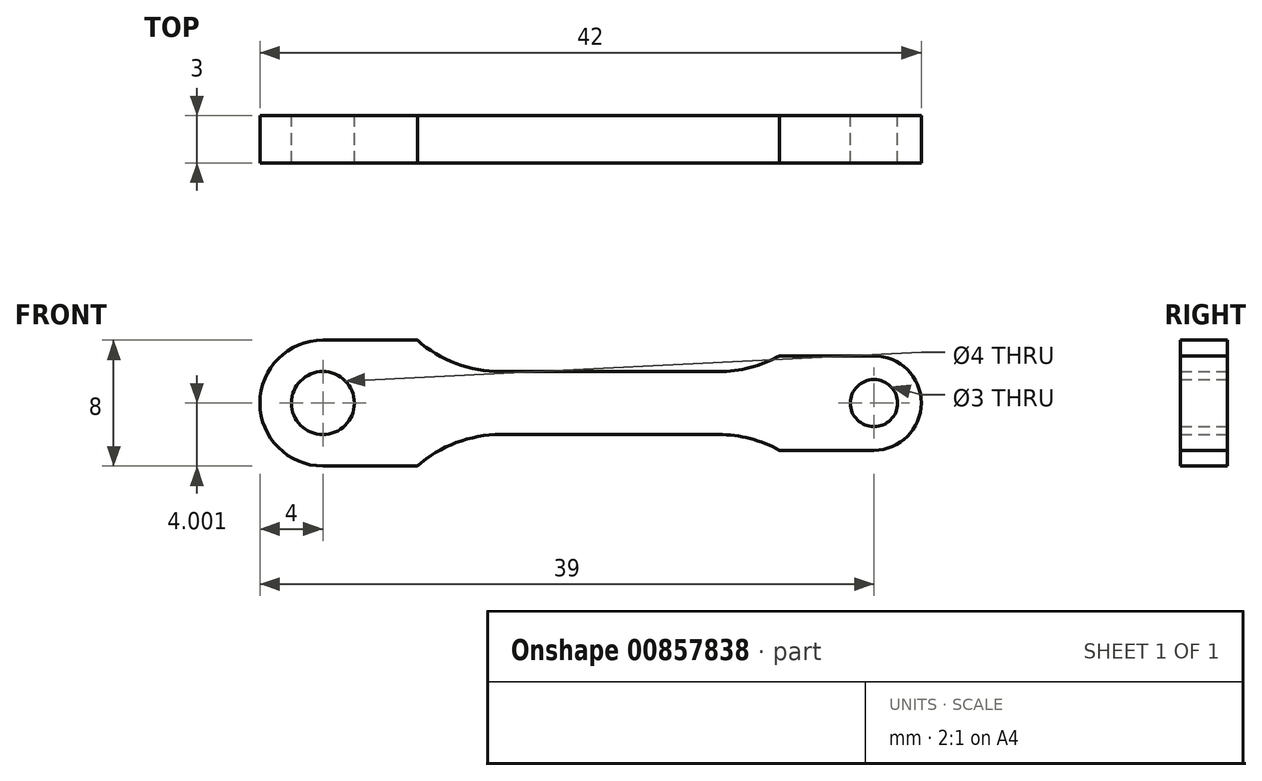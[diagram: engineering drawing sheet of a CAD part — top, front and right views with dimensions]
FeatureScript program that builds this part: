
annotation { "Feature Type Name" : "Feature", "Feature Type Description" : "" }
export const myFeature = defineFeature(function(context is Context, id is Id, definition is map)
    precondition{}
    {
        {
            var Q0;
            Q0=qCreatedBy(makeId("Front.planeOp"),FACE);
            var sketch = newSketch(context, id + "F0", { "sketchPlane" : qUnion([Q0])});
            skCircle(sketch, "E0", {"center": v(22.61, 11.46) * mm, "radius": 2 * mm});
            skCircle(sketch, "E1", {"center": v(57.61, 11.46) * mm, "radius": 1.5 * mm});
            skArc(sketch, "E2", {"start": v(22.61, 15.46) * mm, "mid": v(18.61, 11.46) * mm, "end": v(22.61, 7.46) * mm});
            skArc(sketch, "E3", {"start": v(57.61, 8.46) * mm, "mid": v(60.61, 11.46) * mm, "end": v(57.61, 14.46) * mm});
            skLineSegment(sketch, "E4", {"start": v(22.61, 7.46) * mm, "end": v(28.61, 7.46) * mm});
            skLineSegment(sketch, "E5", {"start": v(22.61, 15.46) * mm, "end": v(28.61, 15.46) * mm});
            skLineSegment(sketch, "E6", {"start": v(57.61, 14.46) * mm, "end": v(51.61, 14.46) * mm});
            skLineSegment(sketch, "E7", {"start": v(57.61, 8.46) * mm, "end": v(51.61, 8.46) * mm});
            skLineSegment(sketch, "E8", {"start": v(22.61, 11.46) * mm, "end": v(67.05, 11.46) * mm, "construction": true});
            skLineSegment(sketch, "E9", {"start": v(33.9, 13.46) * mm, "end": v(47.74, 13.46) * mm});
            skLineSegment(sketch, "E10", {"start": v(33.9, 9.46) * mm, "end": v(47.74, 9.46) * mm});
            skPoint(sketch, "E11", {"position": v(33.9, 1.46) * mm});
            skArc(sketch, "E12", {"start": v(33.9, 9.46) * mm, "mid": v(31.07, 8.94) * mm, "end": v(28.61, 7.46) * mm});
            skPoint(sketch, "E13.MirrorP", {"position": v(33.9, 21.46) * mm});
            skArc(sketch, "E14", {"start": v(33.9, 13.46) * mm, "mid": v(31.07, 13.98) * mm, "end": v(28.61, 15.46) * mm});
            skPoint(sketch, "E15", {"position": v(47.74, 1.46) * mm});
            skArc(sketch, "E16", {"start": v(47.74, 9.46) * mm, "mid": v(49.74, 9.2) * mm, "end": v(51.61, 8.46) * mm});
            skArc(sketch, "E17.MirrorCS", {"start": v(47.74, 13.46) * mm, "mid": v(49.74, 13.72) * mm, "end": v(51.61, 14.46) * mm});
            skSolve(sketch);
        }
        {
            var Q0;
            Q0=makeQuery(id+"F0.imprint","IMPRINT",FACE,{"disambiguationData":[TD([[makeQuery(id+"F0.imprint","IMPRINT",EDGE,{"derivedFrom":sQuery(id+"F0.wireOp",EDGE,"E0")}),-1.0]])]});
            extrude(context, id + "F1", {"entities" : qUnion([Q0]), "depth" : 3 * mm, "offsetDistance" : 25 * mm});
        }
    });
